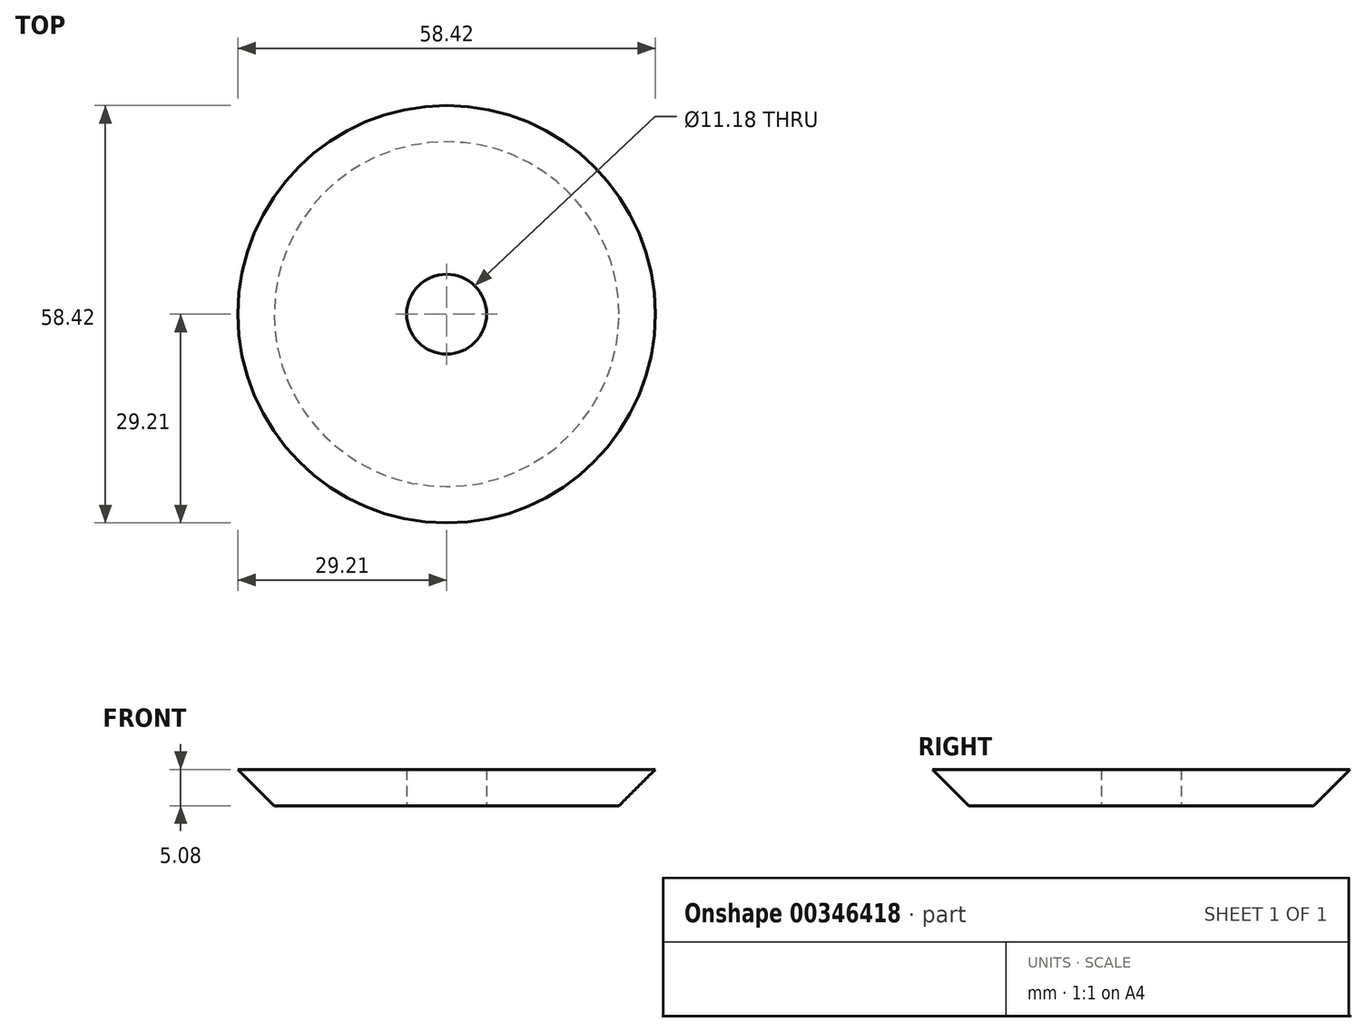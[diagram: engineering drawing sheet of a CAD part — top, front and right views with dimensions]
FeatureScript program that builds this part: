
annotation { "Feature Type Name" : "Feature", "Feature Type Description" : "" }
export const myFeature = defineFeature(function(context is Context, id is Id, definition is map)
    precondition{}
    {
        {
            var Q0;
            Q0=qCreatedBy(makeId("Top.planeOp"),FACE);
            var sketch = newSketch(context, id + "F0", { "sketchPlane" : qUnion([Q0])});
            skCircle(sketch, "E0", {"center": v(0, 0) * mm, "radius": 5.59 * mm});
            skCircle(sketch, "E1", {"center": v(0, 0) * mm, "radius": 29.21 * mm});
            skSolve(sketch);
        }
        {
            var Q0;
            Q0=makeQuery(id+"F0.imprint","IMPRINT",FACE,{"disambiguationData":[TD([[makeQuery(id+"F0.imprint","IMPRINT",EDGE,{"derivedFrom":sQuery(id+"F0.wireOp",EDGE,"E0")}),-1.0]])]});
            extrude(context, id + "F1", {"entities" : qUnion([Q0]), "depth" : 5.08 * mm, "offsetDistance" : 25.4 * mm});
        }
        {
            var Q0;
            Q0=makeQuery(id+"F1.opExtrude","CAP_EDGE",EDGE,{"disambiguationData":[OSD([sQuery(id+"F0.wireOp",EDGE,"E1")])],"isStart":true});
            chamfer(context, id + "F2", {"entities" : qUnion([Q0]), "width" : 5.08 * mm, "tangentPropagation" : true});
        }
    });
